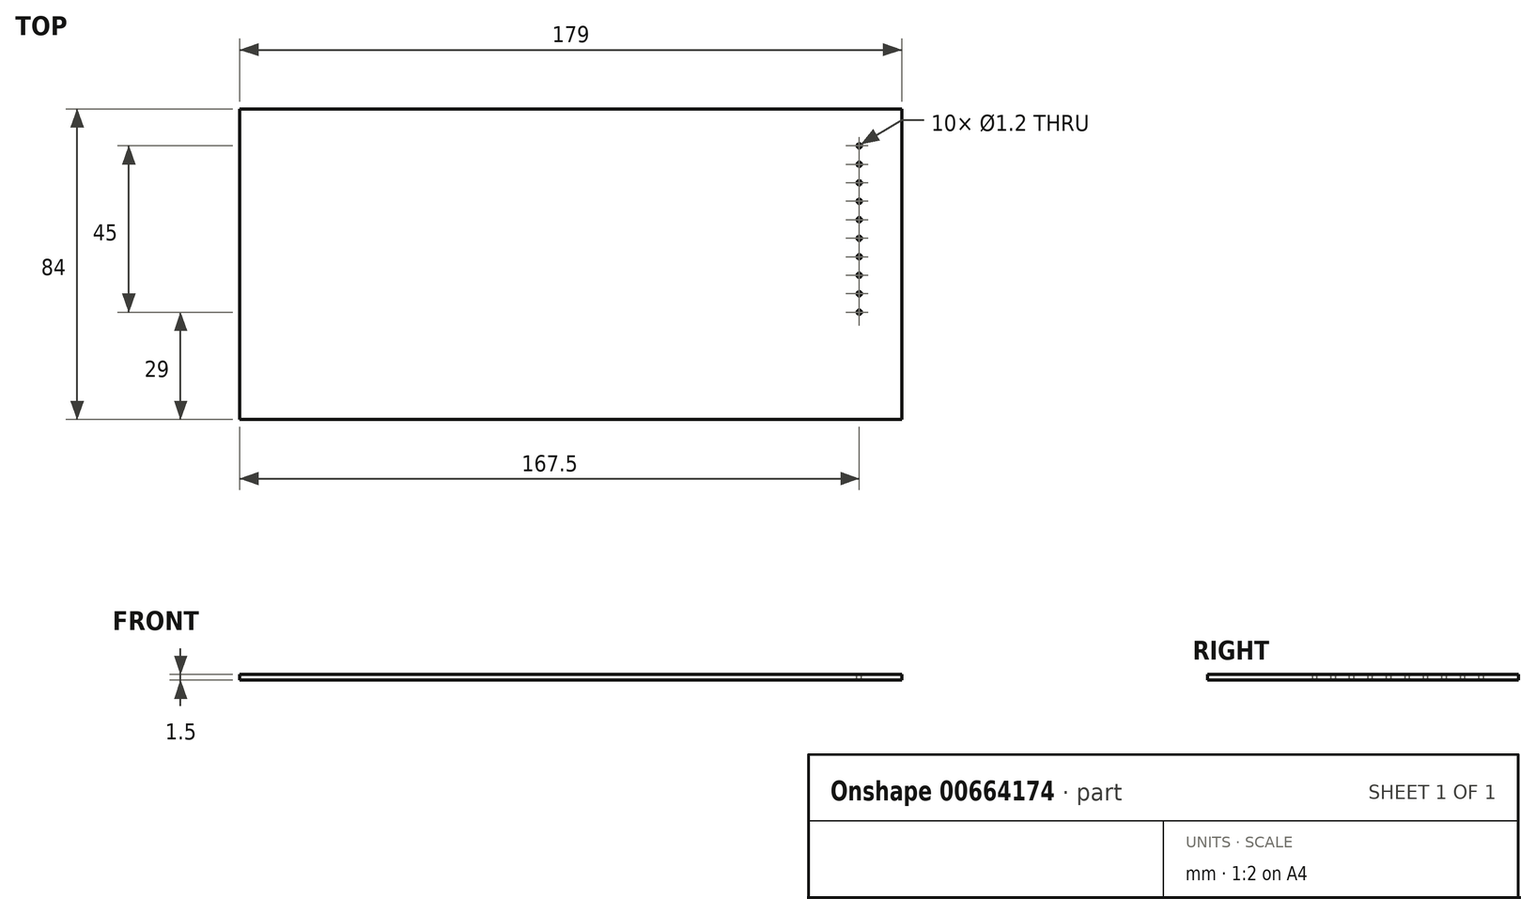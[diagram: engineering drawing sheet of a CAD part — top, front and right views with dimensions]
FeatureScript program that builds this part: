
annotation { "Feature Type Name" : "Feature", "Feature Type Description" : "" }
export const myFeature = defineFeature(function(context is Context, id is Id, definition is map)
    precondition{}
    {
        {
            var Q0;
            Q0=qCreatedBy(makeId("Top.planeOp"),FACE);
            var sketch = newSketch(context, id + "F0", { "sketchPlane" : qUnion([Q0])});
            skLineSegment(sketch, "E0.bottom", {"start": v(-89.5, 42) * mm, "end": v(89.5, 42) * mm});
            skLineSegment(sketch, "E0.top", {"start": v(-89.5, -42) * mm, "end": v(89.5, -42) * mm});
            skLineSegment(sketch, "E0.left", {"start": v(-89.5, 42) * mm, "end": v(-89.5, -42) * mm});
            skLineSegment(sketch, "E0.right", {"start": v(89.5, 42) * mm, "end": v(89.5, -42) * mm});
            skLineSegment(sketch, "E1", {"start": v(0, 42) * mm, "end": v(0, -42) * mm, "construction": true});
            skLineSegment(sketch, "E2.bottom", {"start": v(-83, -42) * mm, "end": v(83, -42) * mm});
            skLineSegment(sketch, "E2.top", {"start": v(-82, -55) * mm, "end": v(82, -55) * mm});
            skLineSegment(sketch, "E2.left", {"start": v(-83, -42) * mm, "end": v(-83, -54) * mm});
            skLineSegment(sketch, "E2.right", {"start": v(83, -42) * mm, "end": v(83, -54) * mm});
            skPoint(sketch, "E3.visualSharp", {"position": v(-83, -55) * mm});
            skArc(sketch, "E3.filletArc", {"start": v(-83, -54) * mm, "mid": v(-82.7, -54.7) * mm, "end": v(-82, -55) * mm});
            skPoint(sketch, "E4.visualSharp", {"position": v(83, -55) * mm});
            skArc(sketch, "E4.filletArc", {"start": v(82, -55) * mm, "mid": v(82.7, -54.7) * mm, "end": v(83, -54) * mm});
            skSolve(sketch);
        }
        {
            var Q0;
            Q0=makeQuery(id+"F0.imprint","IMPRINT",FACE,{"disambiguationData":[TD([[makeQuery(id+"F0.imprint","IMPRINT",EDGE,{"derivedFrom":sQuery(id+"F0.wireOp",EDGE,"E2.bottom")}),-1.0]])]});
            var Q1;
            Q1=makeQuery(id+"F0.imprint","IMPRINT",FACE,{"disambiguationData":[TD([[makeQuery(id+"F0.imprint","IMPRINT",EDGE,{"derivedFrom":sQuery(id+"F0.wireOp",EDGE,"E0.bottom")}),-1.0]])]});
            extrude(context, id + "F1", {"entities" : qUnion([Q0, Q1]), "depth" : 1.5 * mm, "offsetDistance" : 25 * mm});
        }
        {
            var Q0;
            Q0=makeQuery(id+"F1.opExtrude","CAP_FACE",FACE,{"disambiguationData":[OSD([sQuery(id+"F0.wireOp",EDGE,"E0.bottom"),sQuery(id+"F0.wireOp",EDGE,"E0.top"),sQuery(id+"F0.wireOp",EDGE,"E0.left"),sQuery(id+"F0.wireOp",EDGE,"E0.right"),sQuery(id+"F0.wireOp",EDGE,"E2.top"),sQuery(id+"F0.wireOp",EDGE,"E2.left"),sQuery(id+"F0.wireOp",EDGE,"E2.right"),sQuery(id+"F0.wireOp",EDGE,"E3.filletArc"),sQuery(id+"F0.wireOp",EDGE,"E4.filletArc")])],"isStart":false});
            var sketch = newSketch(context, id + "F2", { "sketchPlane" : qUnion([Q0])});
            skLineSegment(sketch, "E5.bottom", {"start": v(-80, -50) * mm, "end": v(-76, -50) * mm});
            skLineSegment(sketch, "E5.top", {"start": v(-80, -55) * mm, "end": v(-76, -55) * mm});
            skLineSegment(sketch, "E5.left", {"start": v(-80, -50) * mm, "end": v(-80, -55) * mm});
            skLineSegment(sketch, "E5.right", {"start": v(-76, -50) * mm, "end": v(-76, -55) * mm});
            skLineSegment(sketch, "E6.1.0.0", {"start": v(-72, -50) * mm, "end": v(-72, -55) * mm});
            skLineSegment(sketch, "E6.1.0.1", {"start": v(-72, -50) * mm, "end": v(-68, -50) * mm});
            skLineSegment(sketch, "E6.1.0.2", {"start": v(-72, -55) * mm, "end": v(-68, -55) * mm});
            skLineSegment(sketch, "E6.1.0.3", {"start": v(-68, -50) * mm, "end": v(-68, -55) * mm});
            skLineSegment(sketch, "E6.2.0.0", {"start": v(-64, -50) * mm, "end": v(-64, -55) * mm});
            skLineSegment(sketch, "E6.2.0.1", {"start": v(-64, -50) * mm, "end": v(-60, -50) * mm});
            skLineSegment(sketch, "E6.2.0.2", {"start": v(-64, -55) * mm, "end": v(-60, -55) * mm});
            skLineSegment(sketch, "E6.2.0.3", {"start": v(-60, -50) * mm, "end": v(-60, -55) * mm});
            skLineSegment(sketch, "E6.3.0.0", {"start": v(-56, -50) * mm, "end": v(-56, -55) * mm});
            skLineSegment(sketch, "E6.3.0.1", {"start": v(-56, -50) * mm, "end": v(-52, -50) * mm});
            skLineSegment(sketch, "E6.3.0.2", {"start": v(-56, -55) * mm, "end": v(-52, -55) * mm});
            skLineSegment(sketch, "E6.3.0.3", {"start": v(-52, -50) * mm, "end": v(-52, -55) * mm});
            skLineSegment(sketch, "E6.4.0.0", {"start": v(-48, -50) * mm, "end": v(-48, -55) * mm});
            skLineSegment(sketch, "E6.4.0.1", {"start": v(-48, -50) * mm, "end": v(-44, -50) * mm});
            skLineSegment(sketch, "E6.4.0.2", {"start": v(-48, -55) * mm, "end": v(-44, -55) * mm});
            skLineSegment(sketch, "E6.4.0.3", {"start": v(-44, -50) * mm, "end": v(-44, -55) * mm});
            skLineSegment(sketch, "E6.5.0.0", {"start": v(-40, -50) * mm, "end": v(-40, -55) * mm});
            skLineSegment(sketch, "E6.5.0.1", {"start": v(-40, -50) * mm, "end": v(-36, -50) * mm});
            skLineSegment(sketch, "E6.5.0.2", {"start": v(-40, -55) * mm, "end": v(-36, -55) * mm});
            skLineSegment(sketch, "E6.5.0.3", {"start": v(-36, -50) * mm, "end": v(-36, -55) * mm});
            skLineSegment(sketch, "E6.6.0.0", {"start": v(-32, -50) * mm, "end": v(-32, -55) * mm});
            skLineSegment(sketch, "E6.6.0.1", {"start": v(-32, -50) * mm, "end": v(-28, -50) * mm});
            skLineSegment(sketch, "E6.6.0.2", {"start": v(-32, -55) * mm, "end": v(-28, -55) * mm});
            skLineSegment(sketch, "E6.6.0.3", {"start": v(-28, -50) * mm, "end": v(-28, -55) * mm});
            skLineSegment(sketch, "E6.7.0.0", {"start": v(-24, -50) * mm, "end": v(-24, -55) * mm});
            skLineSegment(sketch, "E6.7.0.1", {"start": v(-24, -50) * mm, "end": v(-20, -50) * mm});
            skLineSegment(sketch, "E6.7.0.2", {"start": v(-24, -55) * mm, "end": v(-20, -55) * mm});
            skLineSegment(sketch, "E6.7.0.3", {"start": v(-20, -50) * mm, "end": v(-20, -55) * mm});
            skLineSegment(sketch, "E6.8.0.0", {"start": v(-16, -50) * mm, "end": v(-16, -55) * mm});
            skLineSegment(sketch, "E6.8.0.1", {"start": v(-16, -50) * mm, "end": v(-12, -50) * mm});
            skLineSegment(sketch, "E6.8.0.2", {"start": v(-16, -55) * mm, "end": v(-12, -55) * mm});
            skLineSegment(sketch, "E6.8.0.3", {"start": v(-12, -50) * mm, "end": v(-12, -55) * mm});
            skLineSegment(sketch, "E6.9.0.0", {"start": v(-8, -50) * mm, "end": v(-8, -55) * mm});
            skLineSegment(sketch, "E6.9.0.1", {"start": v(-8, -50) * mm, "end": v(-4, -50) * mm});
            skLineSegment(sketch, "E6.9.0.2", {"start": v(-8, -55) * mm, "end": v(-4, -55) * mm});
            skLineSegment(sketch, "E6.9.0.3", {"start": v(-4, -50) * mm, "end": v(-4, -55) * mm});
            skLineSegment(sketch, "E6.10.0.0", {"start": v(0, -50) * mm, "end": v(0, -55) * mm});
            skLineSegment(sketch, "E6.10.0.1", {"start": v(0, -50) * mm, "end": v(4, -50) * mm});
            skLineSegment(sketch, "E6.10.0.2", {"start": v(0, -55) * mm, "end": v(4, -55) * mm});
            skLineSegment(sketch, "E6.10.0.3", {"start": v(4, -50) * mm, "end": v(4, -55) * mm});
            skLineSegment(sketch, "E6.11.0.0", {"start": v(8, -50) * mm, "end": v(8, -55) * mm});
            skLineSegment(sketch, "E6.11.0.1", {"start": v(8, -50) * mm, "end": v(12, -50) * mm});
            skLineSegment(sketch, "E6.11.0.2", {"start": v(8, -55) * mm, "end": v(12, -55) * mm});
            skLineSegment(sketch, "E6.11.0.3", {"start": v(12, -50) * mm, "end": v(12, -55) * mm});
            skLineSegment(sketch, "E6.12.0.0", {"start": v(16, -50) * mm, "end": v(16, -55) * mm});
            skLineSegment(sketch, "E6.12.0.1", {"start": v(16, -50) * mm, "end": v(20, -50) * mm});
            skLineSegment(sketch, "E6.12.0.2", {"start": v(16, -55) * mm, "end": v(20, -55) * mm});
            skLineSegment(sketch, "E6.12.0.3", {"start": v(20, -50) * mm, "end": v(20, -55) * mm});
            skLineSegment(sketch, "E6.13.0.0", {"start": v(24, -50) * mm, "end": v(24, -55) * mm});
            skLineSegment(sketch, "E6.13.0.1", {"start": v(24, -50) * mm, "end": v(28, -50) * mm});
            skLineSegment(sketch, "E6.13.0.2", {"start": v(24, -55) * mm, "end": v(28, -55) * mm});
            skLineSegment(sketch, "E6.13.0.3", {"start": v(28, -50) * mm, "end": v(28, -55) * mm});
            skLineSegment(sketch, "E6.14.0.0", {"start": v(32, -50) * mm, "end": v(32, -55) * mm});
            skLineSegment(sketch, "E6.14.0.1", {"start": v(32, -50) * mm, "end": v(36, -50) * mm});
            skLineSegment(sketch, "E6.14.0.2", {"start": v(32, -55) * mm, "end": v(36, -55) * mm});
            skLineSegment(sketch, "E6.14.0.3", {"start": v(36, -50) * mm, "end": v(36, -55) * mm});
            skLineSegment(sketch, "E6.15.0.0", {"start": v(40, -50) * mm, "end": v(40, -55) * mm});
            skLineSegment(sketch, "E6.15.0.1", {"start": v(40, -50) * mm, "end": v(44, -50) * mm});
            skLineSegment(sketch, "E6.15.0.2", {"start": v(40, -55) * mm, "end": v(44, -55) * mm});
            skLineSegment(sketch, "E6.15.0.3", {"start": v(44, -50) * mm, "end": v(44, -55) * mm});
            skLineSegment(sketch, "E6.16.0.0", {"start": v(48, -50) * mm, "end": v(48, -55) * mm});
            skLineSegment(sketch, "E6.16.0.1", {"start": v(48, -50) * mm, "end": v(52, -50) * mm});
            skLineSegment(sketch, "E6.16.0.2", {"start": v(48, -55) * mm, "end": v(52, -55) * mm});
            skLineSegment(sketch, "E6.16.0.3", {"start": v(52, -50) * mm, "end": v(52, -55) * mm});
            skLineSegment(sketch, "E6.17.0.0", {"start": v(56, -50) * mm, "end": v(56, -55) * mm});
            skLineSegment(sketch, "E6.17.0.1", {"start": v(56, -50) * mm, "end": v(60, -50) * mm});
            skLineSegment(sketch, "E6.17.0.2", {"start": v(56, -55) * mm, "end": v(60, -55) * mm});
            skLineSegment(sketch, "E6.17.0.3", {"start": v(60, -50) * mm, "end": v(60, -55) * mm});
            skLineSegment(sketch, "E6.18.0.0", {"start": v(64, -50) * mm, "end": v(64, -55) * mm});
            skLineSegment(sketch, "E6.18.0.1", {"start": v(64, -50) * mm, "end": v(68, -50) * mm});
            skLineSegment(sketch, "E6.18.0.2", {"start": v(64, -55) * mm, "end": v(68, -55) * mm});
            skLineSegment(sketch, "E6.18.0.3", {"start": v(68, -50) * mm, "end": v(68, -55) * mm});
            skLineSegment(sketch, "E6.19.0.0", {"start": v(72, -50) * mm, "end": v(72, -55) * mm});
            skLineSegment(sketch, "E6.19.0.1", {"start": v(72, -50) * mm, "end": v(76, -50) * mm});
            skLineSegment(sketch, "E6.19.0.2", {"start": v(72, -55) * mm, "end": v(76, -55) * mm});
            skLineSegment(sketch, "E6.19.0.3", {"start": v(76, -50) * mm, "end": v(76, -55) * mm});
            skLineSegment(sketch, "E6.direction1", {"start": v(-80, -55) * mm, "end": v(-72, -55) * mm, "construction": true});
            skCircle(sketch, "E7", {"center": v(78, 32) * mm, "radius": 0.6 * mm});
            skCircle(sketch, "E8.0.1.0", {"center": v(78, 27) * mm, "radius": 0.6 * mm});
            skCircle(sketch, "E8.0.2.0", {"center": v(78, 22) * mm, "radius": 0.6 * mm});
            skCircle(sketch, "E8.0.3.0", {"center": v(78, 17) * mm, "radius": 0.6 * mm});
            skCircle(sketch, "E8.0.4.0", {"center": v(78, 12) * mm, "radius": 0.6 * mm});
            skCircle(sketch, "E8.0.5.0", {"center": v(78, 7) * mm, "radius": 0.6 * mm});
            skCircle(sketch, "E8.0.6.0", {"center": v(78, 2) * mm, "radius": 0.6 * mm});
            skCircle(sketch, "E8.0.7.0", {"center": v(78, -3) * mm, "radius": 0.6 * mm});
            skCircle(sketch, "E8.0.8.0", {"center": v(78, -8) * mm, "radius": 0.6 * mm});
            skCircle(sketch, "E8.0.9.0", {"center": v(78, -13) * mm, "radius": 0.6 * mm});
            skLineSegment(sketch, "E8.direction1", {"start": v(78, 32) * mm, "end": v(94.5, 32) * mm, "construction": true});
            skLineSegment(sketch, "E8.direction2", {"start": v(78, 32) * mm, "end": v(78, 27) * mm, "construction": true});
            skPoint(sketch, "E9.endSnap0", {"position": v(56, -52.5) * mm});
            skLineSegment(sketch, "E10.bottom", {"start": v(76, -50) * mm, "end": v(72, -50) * mm});
            skLineSegment(sketch, "E10.top", {"start": v(76, -10) * mm, "end": v(72, -10) * mm});
            skLineSegment(sketch, "E10.left", {"start": v(76, -50) * mm, "end": v(76, -10) * mm});
            skLineSegment(sketch, "E10.right", {"start": v(72, -50) * mm, "end": v(72, -10) * mm});
            skLineSegment(sketch, "E11.bottom", {"start": v(80, -10) * mm, "end": v(76, -10) * mm});
            skLineSegment(sketch, "E11.top", {"start": v(80, -6) * mm, "end": v(76, -6) * mm});
            skLineSegment(sketch, "E11.left", {"start": v(80, -10) * mm, "end": v(80, -6) * mm});
            skLineSegment(sketch, "E11.right", {"start": v(76, -10) * mm, "end": v(76, -6) * mm});
            skLineSegment(sketch, "E12", {"start": v(76, -10) * mm, "end": v(76, -10) * mm});
            skLineSegment(sketch, "E13", {"start": v(72, -10) * mm, "end": v(76, -6) * mm});
            skLineSegment(sketch, "E14.top", {"start": v(64, -8) * mm, "end": v(68, -8) * mm});
            skLineSegment(sketch, "E14.left", {"start": v(64, -50) * mm, "end": v(64, -8) * mm});
            skLineSegment(sketch, "E14.right", {"start": v(68, -50) * mm, "end": v(68, -8) * mm});
            skLineSegment(sketch, "E15.bottom", {"start": v(80, 0) * mm, "end": v(76, 0) * mm});
            skLineSegment(sketch, "E15.top", {"start": v(80, 4) * mm, "end": v(76, 4) * mm});
            skLineSegment(sketch, "E15.left", {"start": v(80, 0) * mm, "end": v(80, 4) * mm});
            skLineSegment(sketch, "E15.right", {"start": v(76, 0) * mm, "end": v(76, 4) * mm});
            skLineSegment(sketch, "E16", {"start": v(68, -8) * mm, "end": v(76, 0) * mm});
            skLineSegment(sketch, "E17", {"start": v(76, 4) * mm, "end": v(64, -8) * mm});
            skLineSegment(sketch, "E18.bottom", {"start": v(80, 10) * mm, "end": v(76, 10) * mm});
            skLineSegment(sketch, "E18.top", {"start": v(80, 14) * mm, "end": v(76, 14) * mm});
            skLineSegment(sketch, "E18.left", {"start": v(80, 10) * mm, "end": v(80, 14) * mm});
            skLineSegment(sketch, "E18.right", {"start": v(76, 10) * mm, "end": v(76, 14) * mm});
            skLineSegment(sketch, "E19.bottom", {"start": v(60, -50) * mm, "end": v(56, -50) * mm});
            skLineSegment(sketch, "E19.top", {"start": v(60, -6) * mm, "end": v(56, -6) * mm});
            skLineSegment(sketch, "E19.left", {"start": v(60, -50) * mm, "end": v(60, -6) * mm});
            skLineSegment(sketch, "E19.right", {"start": v(56, -50) * mm, "end": v(56, -6) * mm});
            skLineSegment(sketch, "E20", {"start": v(56, -6) * mm, "end": v(76, 14) * mm});
            skLineSegment(sketch, "E21", {"start": v(60, -6) * mm, "end": v(76, 10) * mm});
            skLineSegment(sketch, "E22.bottom", {"start": v(80, 20) * mm, "end": v(76, 20) * mm});
            skLineSegment(sketch, "E22.top", {"start": v(80, 24) * mm, "end": v(76, 24) * mm});
            skLineSegment(sketch, "E22.left", {"start": v(80, 20) * mm, "end": v(80, 24) * mm});
            skLineSegment(sketch, "E22.right", {"start": v(76, 20) * mm, "end": v(76, 24) * mm});
            skLineSegment(sketch, "E23.bottom", {"start": v(80, 30) * mm, "end": v(76, 30) * mm});
            skLineSegment(sketch, "E23.top", {"start": v(80, 34) * mm, "end": v(76, 34) * mm});
            skLineSegment(sketch, "E23.left", {"start": v(80, 30) * mm, "end": v(80, 34) * mm});
            skLineSegment(sketch, "E23.right", {"start": v(76, 30) * mm, "end": v(76, 34) * mm});
            skLineSegment(sketch, "E24.top", {"start": v(48, -4) * mm, "end": v(52, -4) * mm});
            skLineSegment(sketch, "E24.left", {"start": v(48, -50) * mm, "end": v(48, -4) * mm});
            skLineSegment(sketch, "E24.right", {"start": v(52, -50) * mm, "end": v(52, -4) * mm});
            skLineSegment(sketch, "E25", {"start": v(52, -4) * mm, "end": v(76, 20) * mm});
            skLineSegment(sketch, "E26", {"start": v(48, -4) * mm, "end": v(76, 24) * mm});
            skLineSegment(sketch, "E27.top", {"start": v(40, -2.53) * mm, "end": v(44, -2.53) * mm});
            skLineSegment(sketch, "E27.left", {"start": v(40, -50) * mm, "end": v(40, -2.53) * mm});
            skLineSegment(sketch, "E27.right", {"start": v(44, -50) * mm, "end": v(44, -2.53) * mm});
            skLineSegment(sketch, "E28", {"start": v(44, -2.53) * mm, "end": v(76, 30) * mm});
            skLineSegment(sketch, "E29", {"start": v(40, -2.53) * mm, "end": v(76, 34) * mm});
            skSolve(sketch);
        }
        {
            var Q0;
            Q0=makeQuery(id+"F2.imprint","IMPRINT",FACE,{"disambiguationData":[TD([[makeQuery(id+"F2.imprint","IMPRINT",EDGE,{"derivedFrom":sQuery(id+"F2.wireOp",EDGE,"E7")}),1.0]])]});
            var Q1;
            Q1=makeQuery(id+"F2.imprint","IMPRINT",FACE,{"disambiguationData":[TD([[makeQuery(id+"F2.imprint","IMPRINT",EDGE,{"derivedFrom":sQuery(id+"F2.wireOp",EDGE,"E8.0.1.0")}),1.0]])]});
            var Q2;
            Q2=makeQuery(id+"F2.imprint","IMPRINT",FACE,{"disambiguationData":[TD([[makeQuery(id+"F2.imprint","IMPRINT",EDGE,{"derivedFrom":sQuery(id+"F2.wireOp",EDGE,"E8.0.2.0")}),1.0]])]});
            var Q3;
            Q3=makeQuery(id+"F2.imprint","IMPRINT",FACE,{"disambiguationData":[TD([[makeQuery(id+"F2.imprint","IMPRINT",EDGE,{"derivedFrom":sQuery(id+"F2.wireOp",EDGE,"E8.0.3.0")}),1.0]])]});
            var Q4;
            Q4=makeQuery(id+"F2.imprint","IMPRINT",FACE,{"disambiguationData":[TD([[makeQuery(id+"F2.imprint","IMPRINT",EDGE,{"derivedFrom":sQuery(id+"F2.wireOp",EDGE,"E8.0.4.0")}),1.0]])]});
            var Q5;
            Q5=makeQuery(id+"F2.imprint","IMPRINT",FACE,{"disambiguationData":[TD([[makeQuery(id+"F2.imprint","IMPRINT",EDGE,{"derivedFrom":sQuery(id+"F2.wireOp",EDGE,"E8.0.5.0")}),1.0]])]});
            var Q6;
            Q6=makeQuery(id+"F2.imprint","IMPRINT",FACE,{"disambiguationData":[TD([[makeQuery(id+"F2.imprint","IMPRINT",EDGE,{"derivedFrom":sQuery(id+"F2.wireOp",EDGE,"E8.0.6.0")}),1.0]])]});
            var Q7;
            Q7=makeQuery(id+"F2.imprint","IMPRINT",FACE,{"disambiguationData":[TD([[makeQuery(id+"F2.imprint","IMPRINT",EDGE,{"derivedFrom":sQuery(id+"F2.wireOp",EDGE,"E8.0.7.0")}),1.0]])]});
            var Q8;
            Q8=makeQuery(id+"F2.imprint","IMPRINT",FACE,{"disambiguationData":[TD([[makeQuery(id+"F2.imprint","IMPRINT",EDGE,{"derivedFrom":sQuery(id+"F2.wireOp",EDGE,"E8.0.8.0")}),1.0]])]});
            var Q9;
            Q9=makeQuery(id+"F2.imprint","IMPRINT",FACE,{"disambiguationData":[TD([[makeQuery(id+"F2.imprint","IMPRINT",EDGE,{"derivedFrom":sQuery(id+"F2.wireOp",EDGE,"E8.0.9.0")}),1.0]])]});
            extrude(context, id + "F3", {"entities" : qUnion([Q0, Q1, Q2, Q3, Q4, Q5, Q6, Q7, Q8, Q9]), "operationType" : NewBodyOperationType.REMOVE, "endBound" : BoundingType.THROUGH_ALL, "oppositeDirection" : true, "depth" : 25 * mm, "offsetDistance" : 25 * mm});
        }
    });
